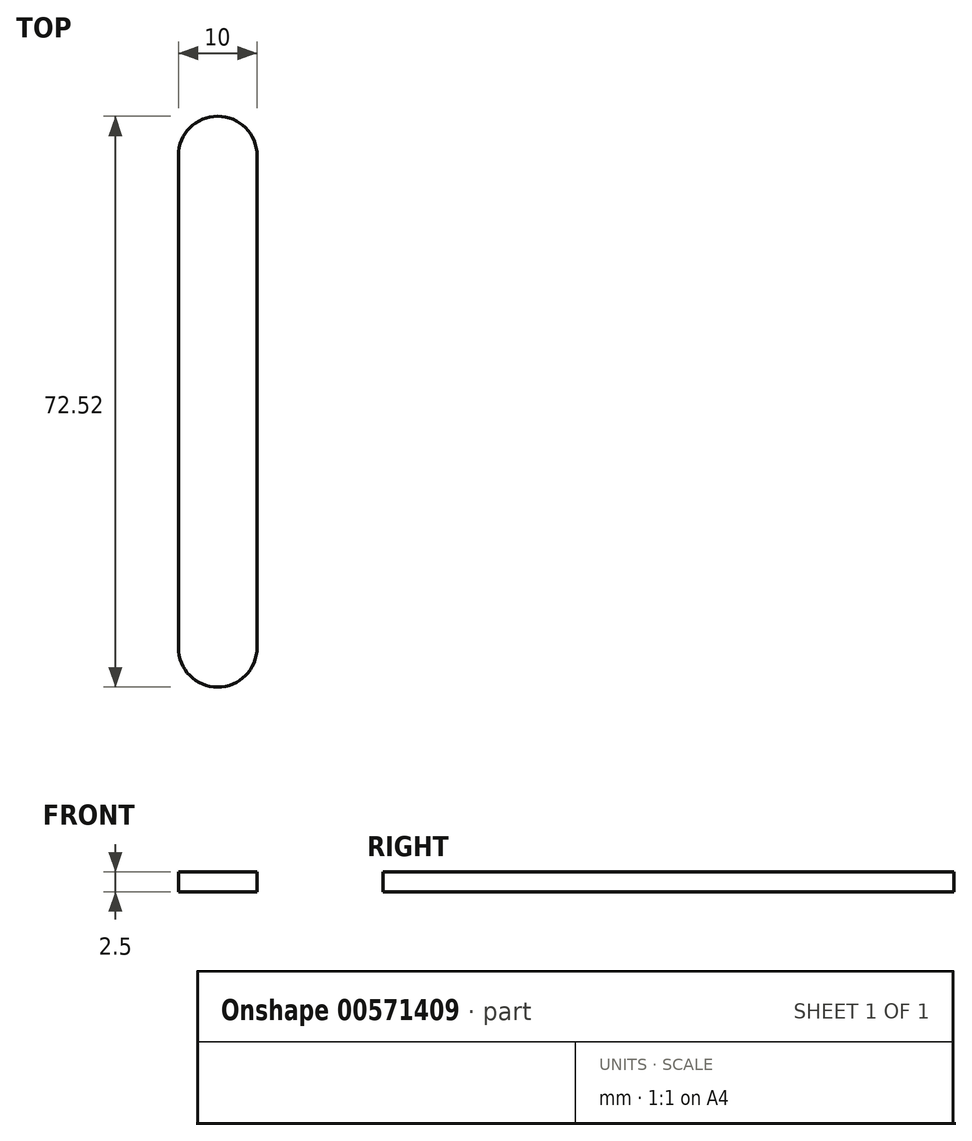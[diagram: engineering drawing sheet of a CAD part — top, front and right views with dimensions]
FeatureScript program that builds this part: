
annotation { "Feature Type Name" : "Feature", "Feature Type Description" : "" }
export const myFeature = defineFeature(function(context is Context, id is Id, definition is map)
    precondition{}
    {
        {
            var Q0;
            Q0=qCreatedBy(makeId("Top.planeOp"),FACE);
            var sketch = newSketch(context, id + "F0", { "sketchPlane" : qUnion([Q0])});
            skLineSegment(sketch, "E0.bottom", {"start": v(5, 36.26) * mm, "end": v(-5, 36.26) * mm});
            skLineSegment(sketch, "E0.top", {"start": v(5, -36.26) * mm, "end": v(-5, -36.26) * mm});
            skLineSegment(sketch, "E0.left", {"start": v(5, 36.26) * mm, "end": v(5, -36.26) * mm});
            skLineSegment(sketch, "E0.right", {"start": v(-5, 36.26) * mm, "end": v(-5, -36.26) * mm});
            skPoint(sketch, "E0.middle", {"position": v(0, 0) * mm});
            skSolve(sketch);
        }
        {
            var Q0;
            Q0=makeQuery(id+"F0.imprint","IMPRINT",FACE,{"disambiguationData":[TD([[makeQuery(id+"F0.imprint","IMPRINT",EDGE,{"derivedFrom":sQuery(id+"F0.wireOp",EDGE,"E0.bottom")}),1.0]])]});
            extrude(context, id + "F1", {"entities" : qUnion([Q0]), "depth" : 2.5 * mm, "offsetDistance" : 25 * mm});
        }
        {
            var Q0;
            Q0=makeQuery(id+"F1.opExtrude","SWEPT_EDGE",EDGE,{"disambiguationData":[OSD([sQuery(id+"F0.wireOp",EDGE,"E0.bottom"),sQuery(id+"F0.wireOp",EDGE,"E0.left")])]});
            var Q1;
            Q1=makeQuery(id+"F1.opExtrude","SWEPT_EDGE",EDGE,{"disambiguationData":[OSD([sQuery(id+"F0.wireOp",EDGE,"E0.bottom"),sQuery(id+"F0.wireOp",EDGE,"E0.right")])]});
            var Q2;
            Q2=makeQuery(id+"F1.opExtrude","SWEPT_EDGE",EDGE,{"disambiguationData":[OSD([sQuery(id+"F0.wireOp",EDGE,"E0.top"),sQuery(id+"F0.wireOp",EDGE,"E0.right")])]});
            var Q3;
            Q3=makeQuery(id+"F1.opExtrude","SWEPT_EDGE",EDGE,{"disambiguationData":[OSD([sQuery(id+"F0.wireOp",EDGE,"E0.top"),sQuery(id+"F0.wireOp",EDGE,"E0.left")])]});
            fillet(context, id + "F2", {"entities" : qUnion([Q0, Q1, Q2, Q3]), "radius" : 5 * mm, "tangentPropagation" : true, "allowEdgeOverflow" : false});
        }
    });
